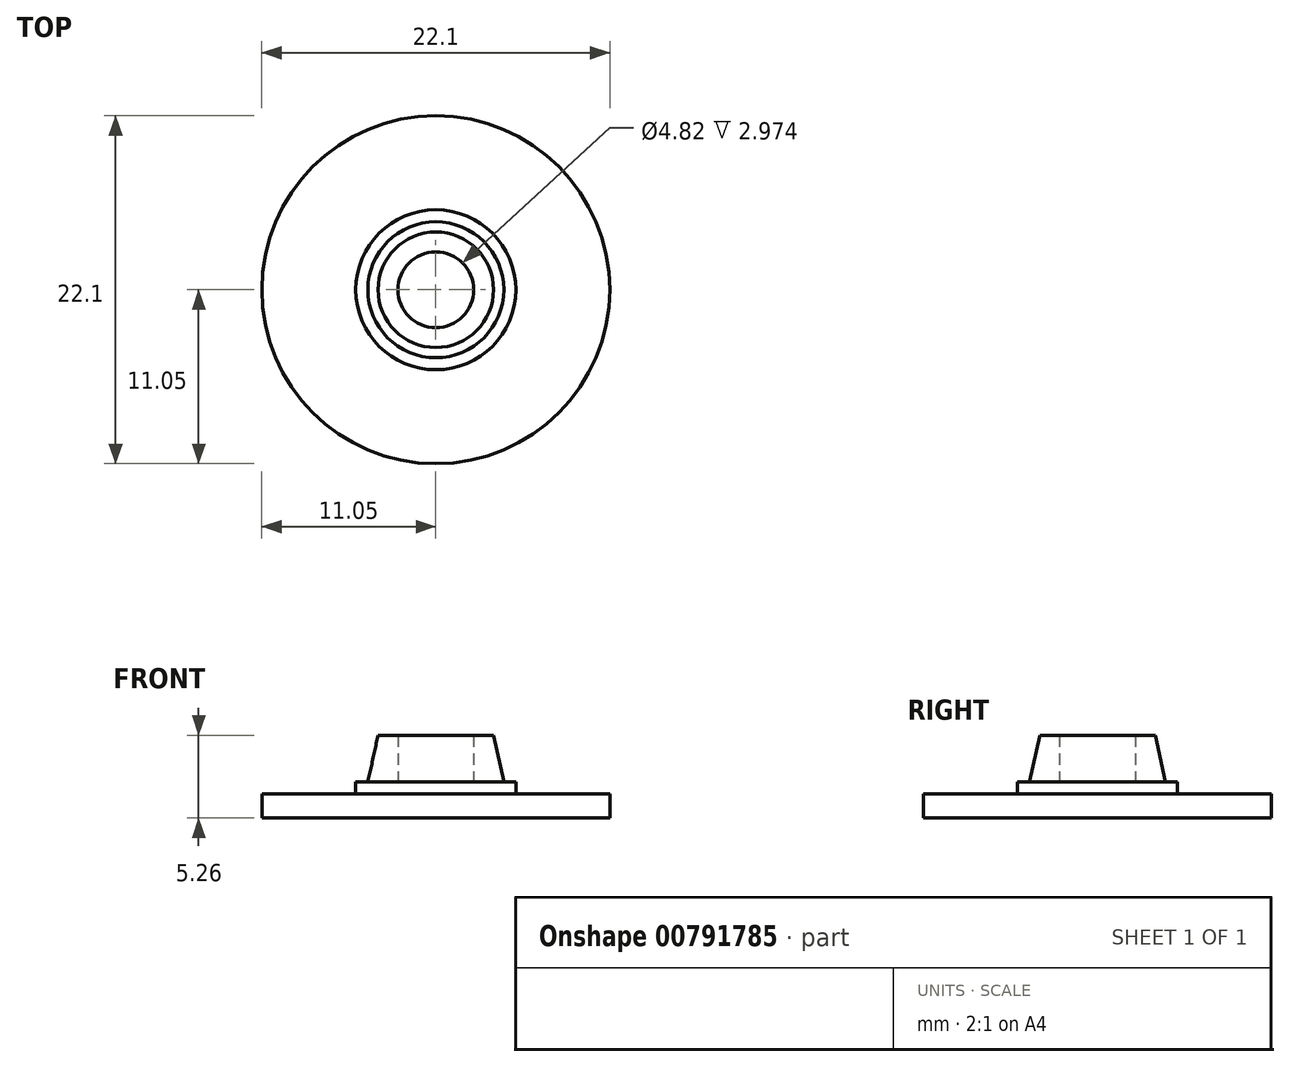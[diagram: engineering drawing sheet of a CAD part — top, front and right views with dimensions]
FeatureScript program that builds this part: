
annotation { "Feature Type Name" : "Feature", "Feature Type Description" : "" }
export const myFeature = defineFeature(function(context is Context, id is Id, definition is map)
    precondition{}
    {
        {
            var Q0;
            Q0=qCreatedBy(makeId("Right.planeOp"),FACE);
            var sketch = newSketch(context, id + "F0", { "sketchPlane" : qUnion([Q0])});
            skLineSegment(sketch, "E0", {"start": v(0, 0) * mm, "end": v(4.32, 0) * mm});
            skLineSegment(sketch, "E1", {"start": v(0, 0) * mm, "end": v(0, 2.97) * mm});
            skLineSegment(sketch, "E2", {"start": v(0, 2.97) * mm, "end": v(3.67, 2.97) * mm});
            skLineSegment(sketch, "E3", {"start": v(4.32, 0) * mm, "end": v(3.67, 2.97) * mm});
            skLineSegment(sketch, "E4", {"start": v(2.4, 2.8) * mm, "end": v(2.4, 2.97) * mm});
            skLineSegment(sketch, "E5", {"start": v(4.32, 0) * mm, "end": v(3.06, -0.17) * mm});
            skLineSegment(sketch, "E6", {"start": v(2.4, 2.8) * mm, "end": v(2.4, 0) * mm});
            skLineSegment(sketch, "E7", {"start": v(2.4, 0) * mm, "end": v(4.32, 0) * mm});
            skSolve(sketch);
        }
        {
            var Q0;
            {var subQ0=sQuery(id+"F0.wireOp",EDGE,"E3");Q0=makeQuery(id+"F0.imprint","IMPRINT",FACE,{"disambiguationData":[TD([[makeQuery(id+"F0.imprint","IMPRINT",EDGE,{"derivedFrom":subQ0}),1.0]])]});}
            var Q1;
            Q1=sQuery(id+"F0.wireOp",EDGE,"E1");
            revolve(context, id + "F1", {"surfaceOperationType" : NewSurfaceOperationType.NEW, "entities" : qUnion([Q0]), "axis" : qUnion([Q1]), "revolveType" : RevolveType.FULL});
        }
        {
            var Q0;
            Q0=qCreatedBy(makeId("Top.planeOp"),FACE);
            var sketch = newSketch(context, id + "F2", { "sketchPlane" : qUnion([Q0])});
            skCircle(sketch, "E8", {"center": v(0, 0) * mm, "radius": 3.94 * mm});
            skCircle(sketch, "E9.0", {"center": v(0, 0) * mm, "radius": 2.67 * mm});
            skSolve(sketch);
        }
        {
            var Q0;
            Q0=qSketchRegion(id+"F2",true);
            extrude(context, id + "F3", {"entities" : qUnion([Q0]), "depth" : 2.8 * mm, "offsetDistance" : 25.4 * mm});
        }
        {
            var Q0;
            Q0=makeQuery(id+"F1.opRevolve","SWEPT_FACE",FACE,{"disambiguationData":[OSD([sQuery(id+"F0.wireOp",EDGE,"E0")])]});
            var sketch = newSketch(context, id + "F4", { "sketchPlane" : qUnion([Q0])});
            skCircle(sketch, "E10", {"center": v(0, 0) * mm, "radius": 5.08 * mm});
            skSolve(sketch);
        }
        {
            var Q0;
            Q0=qSketchRegion(id+"F4",true);
            extrude(context, id + "F5", {"entities" : qUnion([Q0]), "depth" : 0.76 * mm, "offsetDistance" : 25.4 * mm});
        }
        {
            var Q0;
            Q0=makeQuery(id+"F5.opExtrude","CAP_FACE",FACE,{"disambiguationData":[OSD([sQuery(id+"F4.wireOp",EDGE,"E10")])],"isStart":false});
            var sketch = newSketch(context, id + "F6", { "sketchPlane" : qUnion([Q0])});
            skCircle(sketch, "E11", {"center": v(0, 0) * mm, "radius": 11.05 * mm});
            skSolve(sketch);
        }
        {
            var Q0;
            Q0=qSketchRegion(id+"F6",true);
            extrude(context, id + "F7", {"entities" : qUnion([Q0]), "operationType" : NewBodyOperationType.ADD, "depth" : 1.52 * mm, "offsetDistance" : 25.4 * mm});
        }
        {
            var Q0;
            Q0=makeQuery(id+"F3.opExtrude","SWEPT_BODY",BODY,{"disambiguationData":[OSD([sQuery(id+"F2.wireOp",EDGE,"E8"),sQuery(id+"F2.wireOp",EDGE,"E9.0")])]});
            deleteBodies(context, id + "F8", {"entities" : qUnion([Q0])});
        }
    });
